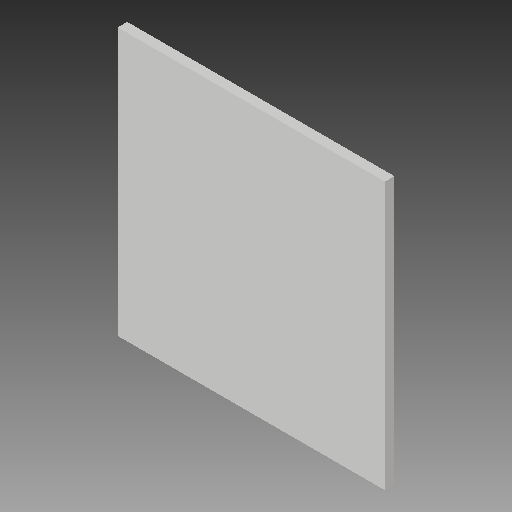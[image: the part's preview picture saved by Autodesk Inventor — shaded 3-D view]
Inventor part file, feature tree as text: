
AUTODESK INVENTOR PART (.ipt)
format: ipt  version: 2018 (Build 220112000, 112)  size: 90,624 bytes
history: native  units: mm
features: sketch x2, other x1, extrude x1
ambient origin geometry x8: Origin, YZ Plane, XZ Plane, XY Plane, X Axis, Y Axis, Z Axis, Center Point
bodies: Body1 (feature_tree)
feature tree (4):
  other  "Bryła1"
  extrude  "Wyciągnięcie proste1"  Depth=168.0mm
  sketch  "Szkic2"
  sketch  "Szkic1"
